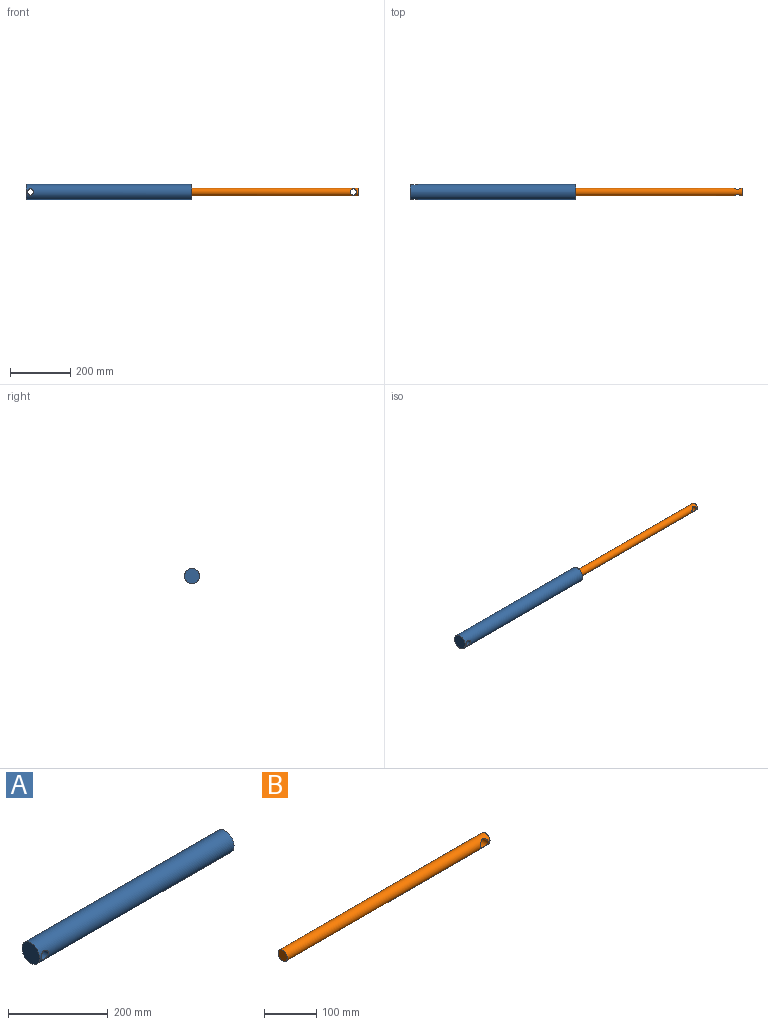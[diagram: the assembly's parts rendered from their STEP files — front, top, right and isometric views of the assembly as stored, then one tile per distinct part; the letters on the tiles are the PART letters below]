
ASSEMBLY  parts=2 mates=1
PART A: 4 faces, bbox 550x50x50 mm
  f0: cylinder r=25mm len=550mm, axis (-1,0,0), area 85718.6mm2, adj f1,f2,f3
  f1: plane 50x50mm, normal (1,0,0), area 1963.5mm2, adj f0
  f2: plane 50x50mm, normal (-1,0,0), area 1963.5mm2, adj f0
  f3: cylinder r=10.25mm len=50mm, axis (0,-1,0), area 3080.3mm2, adj f0
PART B: 4 faces, bbox 550x25x25 mm
  f0: cylinder r=12.5mm len=550mm, axis (-1,0,0), area 42458.1mm2, adj f1,f2,f3
  f1: plane 25x25mm, normal (1,0,0), area 490.9mm2, adj f0
  f2: plane 25x25mm, normal (-1,0,0), area 490.9mm2, adj f0
  f3: cylinder r=10.25mm len=25mm, axis (0,-1,0), area 1289.5mm2, adj f0
PLACE A at identity
PLACE B at identity
MATE slider A.f0 <-> B.f0  axis (1,0,0) through (550,0,0)mm
